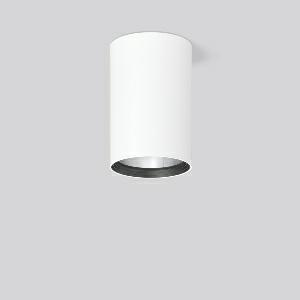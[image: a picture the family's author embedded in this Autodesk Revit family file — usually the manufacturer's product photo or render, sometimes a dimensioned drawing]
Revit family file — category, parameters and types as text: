
# Revit family: heledon_maxi_a_931226_002_1_76_79e3
name_source: partatom
category: Lighting Fixtures
units: mm (PartAtom-declared; Revit-internal decimal feet)

## family parameters
Cut with Voids When Loaded = No
Host = Face
Light Source = No
Part Type = Normal
Room Calculation Point = No
Round Connector Dimension = Use Diameter
Shared = No

## types (1)
- HELEDON maxi A (1 x LED Modul 940, 4400 lm, 4000)
    Apparent Load = 35 VA
    Approval mark = CE
    CIE Flux Codes = 97 100 100 100 100
    Color Rendering = 92
    Color Temperature = 4000
    Default Elevation = 1800 mm
    Description = Series: HELEDON maxi
Cylindrical surface-mounted downlight. Housing: die-cast aluminium, powder-coated. Internal ceiling frame polycarbonate with bayonet mounting. Black plastic ring and recessed LED to prevent glare from the side. Optical assembly with reflector made of MIRO-Silver with 98% total light reflection for outstanding efficiency - can be changed without tools. Best colour rendering index Ra>90. Suitable for Ceiling mounting. Easy installation with a separate ceiling frame with bayonet mounting and plug connection. Driver integrated. Connected via plug-in connector. High quality converter without flickering and stroboscopic effect. The following accessories can be mounted without use of tools: interchangeable lenses, decorative glasses, honeycomb louvre, clear and frosted diffusers, white interchangeable plastic ring. 
Colour: traffic white, matt (RAL 9016)
Diameter: 123 mm
Height: 183 mm
Lamp: LED
Socket: without socket
Colour temperature: 4000K
Colour rendering index (CRI): 92
System power: 35 W
Rated luminous flux: 4400 lm
Luminous efficiency: 126 lm/W
Control gear: Converter, dimmable, DALI
Protection class: I
Type of protection: IP 20
    Height = 183 mm
    Lamp = 1 x LED Modul 940
    Lamp Light Flux = 4400 lm
    Lamp count = 1
    Length = 123 mm
    Lifetime = 50000 h
    Luminous efficacy = 126 lm/W
    Manufacturer = RZB
    ModVariant = No
    Model = 931226.002.1.76
    Mounting Place = Ceiling
    Mounting Type = Surface mounted
    Number of Poles = 1
    OnlyDefault = Yes
    Power Factor = 1
    Product Name = HELEDON maxi A
    Product group = Surface mounted downlights
    ProductGroupID = 302
    Protection Class = Protection class I
    Protection Degree = IP 20
    RLX_Detail_Level = 1
    RLX_Emergency_Light_Flux = 0 lm
    RLX_Emergency_Type = 0
    RLX_Emergency_Type_DB = No
    RlxData = <blob elided: 97145 chars, md5=95569c77>
    Socket = socket
    Standby Power = 0 W
    System Light Flux = 4400 lm
    System Power = 35 W
    Type Comments = Product without accessories
    Type Image = 931192.002.jpg
    URL = http://relux.com
    VarID = ---
    Voltage = 230 V
    Voltage Range = 220-240 V
    Weight = 0.00 kg
    Width = 0 mm  [stored 0 ft]

note: [stored X ft] marks values corroborated as IEEE doubles in the binary element streams (Revit-internal decimal feet)

## geometry (parser evidence)
native form markers: Blend x4, Sweep x10
no freeform markers — native parametric forms only
